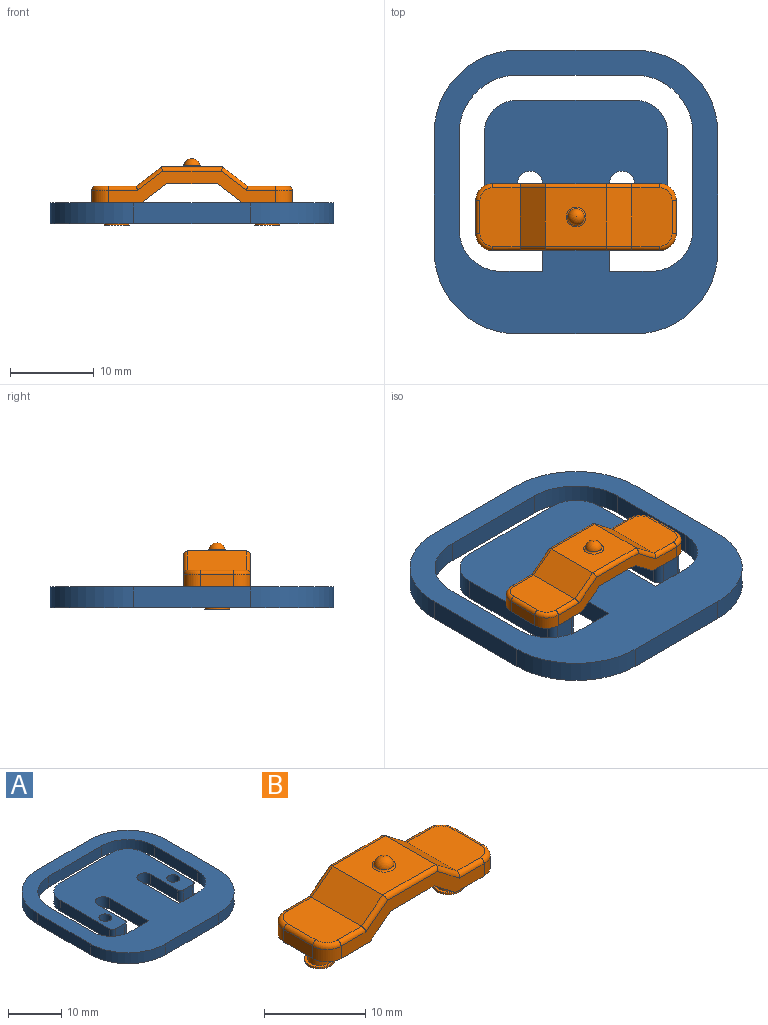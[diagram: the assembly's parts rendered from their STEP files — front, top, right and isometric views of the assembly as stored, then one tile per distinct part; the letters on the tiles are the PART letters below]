
ASSEMBLY  parts=2 mates=1
PART A: 38 faces, bbox 34x34x2.5 mm
  f0: plane 14x2.5mm, normal (0,1,0), area 35mm2, adj f1,f35,f36,f37
  f1: cylinder r=10mm len=10mm, axis (0,0,-1), area 39.3mm2, adj f0,f2,f36,f37
  f2: plane 14x2.5mm, normal (-1,0,0), area 35mm2, adj f1,f3,f36,f37
  f3: cylinder r=10mm len=10mm, axis (0,0,-1), area 39.3mm2, adj f2,f4,f36,f37
  f4: plane 14x2.5mm, normal (0,-1,0), area 35mm2, adj f3,f5,f36,f37
  f5: cylinder r=10mm len=10mm, axis (0,0,-1), area 39.3mm2, adj f4,f6,f36,f37
  f6: plane 14x2.5mm, normal (1,0,0), area 35mm2, adj f5,f35,f36,f37
  f7: plane 10.5x2.5mm, normal (-1,0,0), area 26.2mm2, adj f8,f34,f36,f37
  f8: plane 5x2.5mm, normal (0,1,0), area 12.5mm2, adj f7,f9,f36,f37
  f9: cylinder r=5mm len=5mm, axis (0,0,-1), area 19.6mm2, adj f8,f10,f36,f37
  f10: plane 11.5x2.5mm, normal (1,0,0), area 28.8mm2, adj f9,f11,f36,f37
  f11: cylinder r=7mm len=7mm, axis (0,0,-1), area 27.5mm2, adj f10,f12,f36,f37
  f12: plane 14x2.5mm, normal (0,-1,0), area 35mm2, adj f11,f13,f36,f37
  f13: cylinder r=7mm len=7mm, axis (0,0,-1), area 27.5mm2, adj f12,f14,f36,f37
  f14: plane 11.5x2.5mm, normal (-1,0,0), area 28.8mm2, adj f13,f15,f36,f37
  f15: cylinder r=5mm len=5mm, axis (0,0,-1), area 19.6mm2, adj f14,f16,f36,f37
  f16: plane 5x2.5mm, normal (0,1,0), area 12.5mm2, adj f15,f17,f36,f37
  f17: plane 10.5x2.5mm, normal (1,0,0), area 26.2mm2, adj f16,f18,f36,f37
  f18: cylinder r=1.5mm len=3mm, axis (0,0,-1), area 11.8mm2, adj f17,f19,f36,f37
  f19: plane 7.2x2.5mm, normal (-1,0,0), area 18mm2, adj f18,f20,f36,f37
  f20: cylinder r=0.8mm len=2.5mm, axis (0,0,-1), area 3.1mm2, adj f19,f21,f36,f37
  f21: plane 2.5x2.4mm, normal (0,-1,0), area 6mm2, adj f20,f22,f36,f37
  f22: cylinder r=0.8mm len=2.5mm, axis (0,0,-1), area 3.1mm2, adj f21,f23,f36,f37
  f23: plane 13.2x2.5mm, normal (1,0,0), area 33mm2, adj f22,f24,f36,f37
  f24: cylinder r=4mm len=4mm, axis (0,0,-1), area 15.7mm2, adj f23,f25,f36,f37
  f25: plane 14x2.5mm, normal (0,1,0), area 35mm2, adj f24,f26,f36,f37
  f26: cylinder r=4mm len=4mm, axis (0,0,-1), area 15.7mm2, adj f25,f27,f36,f37
  f27: plane 13.2x2.5mm, normal (-1,0,0), area 33mm2, adj f26,f28,f36,f37
  f28: cylinder r=0.8mm len=2.5mm, axis (0,0,-1), area 3.1mm2, adj f27,f29,f36,f37
  f29: plane 2.5x2.4mm, normal (0,-1,0), area 6mm2, adj f28,f30,f36,f37
  f30: cylinder r=0.8mm len=2.5mm, axis (0,0,-1), area 3.1mm2, adj f29,f31,f36,f37
  f31: plane 7.2x2.5mm, normal (1,0,0), area 18mm2, adj f30,f34,f36,f37
  f32: cylinder r=1.2mm len=2.5mm, axis (0,0,-1), area 18.8mm2, adj f36,f37
  f33: cylinder r=1.2mm len=2.5mm, axis (0,0,-1), area 18.8mm2, adj f36,f37
  f34: cylinder r=1.5mm len=3mm, axis (0,0,-1), area 11.8mm2, adj f7,f31,f36,f37
  f35: cylinder r=10mm len=10mm, axis (0,0,-1), area 39.3mm2, adj f0,f6,f36,f37
  f36: plane 34x34mm, normal (0,0,1), area 788.4mm2, adj f0,f1,f2,f3,f4,f5,f6,f7
  f37: plane 34x34mm, normal (0,0,-1), area 788.4mm2, adj f0,f1,f2,f3,f4,f5,f6,f7
PART B: 44 faces, bbox 24.3x8.3x8 mm
  f0: plane 8x6mm, normal (0,0,-1), area 41.8mm2, adj f1,f11,f12,f13,f15,f17,f36
  f1: plane 8x3mm, normal (0.61,0,-0.79), area 30.2mm2, adj f0,f2,f12,f13
  f2: plane 8x6mm, normal (0,0,-1), area 48mm2, adj f1,f3,f12,f13
  f3: plane 8x3mm, normal (-0.61,0,-0.79), area 30.2mm2, adj f2,f4,f12,f13
  f4: plane 8x6mm, normal (0,0,-1), area 41.8mm2, adj f3,f5,f12,f13,f14,f16,f37
  f5: plane 4x1.5mm, normal (1,0,0), area 6mm2, adj f4,f14,f16,f22
  f6: plane 7x4.82mm, normal (0,0,1), area 32.8mm2, adj f7,f18,f20,f22,f24,f26
  f7: plane 7x3mm, normal (0.61,0,0.79), area 26.5mm2, adj f6,f8,f19,f28
  f8: plane 7.36x7mm, normal (0,0,1), area 47.1mm2, adj f7,f9,f21,f30,f35
  f9: plane 7x3mm, normal (-0.61,0,0.79), area 26.5mm2, adj f8,f10,f23,f32
  f10: plane 7x4.82mm, normal (0,0,1), area 32.8mm2, adj f9,f25,f27,f29,f31,f33
  f11: plane 4x1.5mm, normal (-1,0,0), area 6mm2, adj f0,f15,f17,f29
  f12: plane 20x3.8mm, normal (0,-1,0), area 32.3mm2, adj f0,f1,f2,f3,f4,f16,f17,f18
  f13: plane 20x3.8mm, normal (0,1,0), area 32.3mm2, adj f0,f1,f2,f3,f4,f14,f15,f26
  f14: cylinder r=2mm len=2mm, axis (0,0,1), area 4.7mm2, adj f4,f5,f13,f24
  f15: cylinder r=2mm len=2mm, axis (0,0,-1), area 4.7mm2, adj f0,f11,f13,f31
  f16: cylinder r=2mm len=2mm, axis (0,0,-1), area 4.7mm2, adj f4,f5,f12,f20
  f17: cylinder r=2mm len=2mm, axis (0,0,1), area 4.7mm2, adj f0,f11,f12,f27
  f18: cylinder r=0.5mm len=3.49mm, axis (1,0,0), area 2.7mm2, adj f6,f12,f19,f20
  f19: cylinder r=0.5mm len=3.44mm, axis (0.79,0,-0.61), area 3mm2, adj f7,f12,f18,f21
  f20: torus R=1.5mm, axis (0,0,1), area 2.2mm2, adj f6,f16,f18,f22
  f21: cylinder r=0.5mm len=7.36mm, axis (1,0,0), area 5.7mm2, adj f8,f12,f19,f23
  f22: cylinder r=0.5mm len=4mm, axis (0,-1,0), area 3.1mm2, adj f5,f6,f20,f24
  f23: cylinder r=0.5mm len=3.44mm, axis (0.79,0,0.61), area 3mm2, adj f9,f12,f21,f25
  f24: torus R=1.5mm, axis (0,0,1), area 2.2mm2, adj f6,f14,f22,f26
  f25: cylinder r=0.5mm len=3.49mm, axis (1,0,0), area 2.7mm2, adj f10,f12,f23,f27
  f26: cylinder r=0.5mm len=3.49mm, axis (-1,0,0), area 2.7mm2, adj f6,f13,f24,f28
  f27: torus R=1.5mm, axis (0,0,1), area 2.2mm2, adj f10,f17,f25,f29
  f28: cylinder r=0.5mm len=3.44mm, axis (-0.79,0,0.61), area 3mm2, adj f7,f13,f26,f30
  f29: cylinder r=0.5mm len=4mm, axis (0,1,0), area 3.1mm2, adj f10,f11,f27,f31
  f30: cylinder r=0.5mm len=7.36mm, axis (-1,0,0), area 5.7mm2, adj f8,f13,f28,f32
  f31: torus R=1.5mm, axis (0,0,1), area 2.2mm2, adj f10,f15,f29,f33
  f32: cylinder r=0.5mm len=3.44mm, axis (-0.79,0,-0.61), area 3mm2, adj f9,f13,f30,f33
  f33: cylinder r=0.5mm len=3.49mm, axis (-1,0,0), area 2.7mm2, adj f10,f13,f31,f32
  f34: sphere r=1mm, area 5.2mm2, adj f35
  f35: torus R=1.18mm, axis (0,0,1), area 1.9mm2, adj f8,f34
  f36: cylinder r=1.2mm len=2.5mm, axis (0,0,1), area 18.8mm2, adj f0,f40
  f37: cylinder r=1.2mm len=2.5mm, axis (0,0,1), area 18.8mm2, adj f4,f43
  f38: cylinder r=1.5mm len=3mm, axis (0,0,1), area 1.9mm2, adj f39,f40
  f39: plane 3x3mm, normal (0,0,-1), area 7.1mm2, adj f38
  f40: plane 3x3mm, normal (0,0,1), area 2.5mm2, adj f36,f38
  f41: cylinder r=1.5mm len=3mm, axis (0,0,1), area 1.9mm2, adj f42,f43
  f42: plane 3x3mm, normal (0,0,-1), area 7.1mm2, adj f41
  f43: plane 3x3mm, normal (0,0,1), area 2.5mm2, adj f37,f41
PLACE A t=(0,0.75,0)mm
PLACE B t=(0,0.75,0)mm
MATE fastened A.f32 <-> B.f36  axis (0,0,1) through (-9,-2.25,2.5)mm
